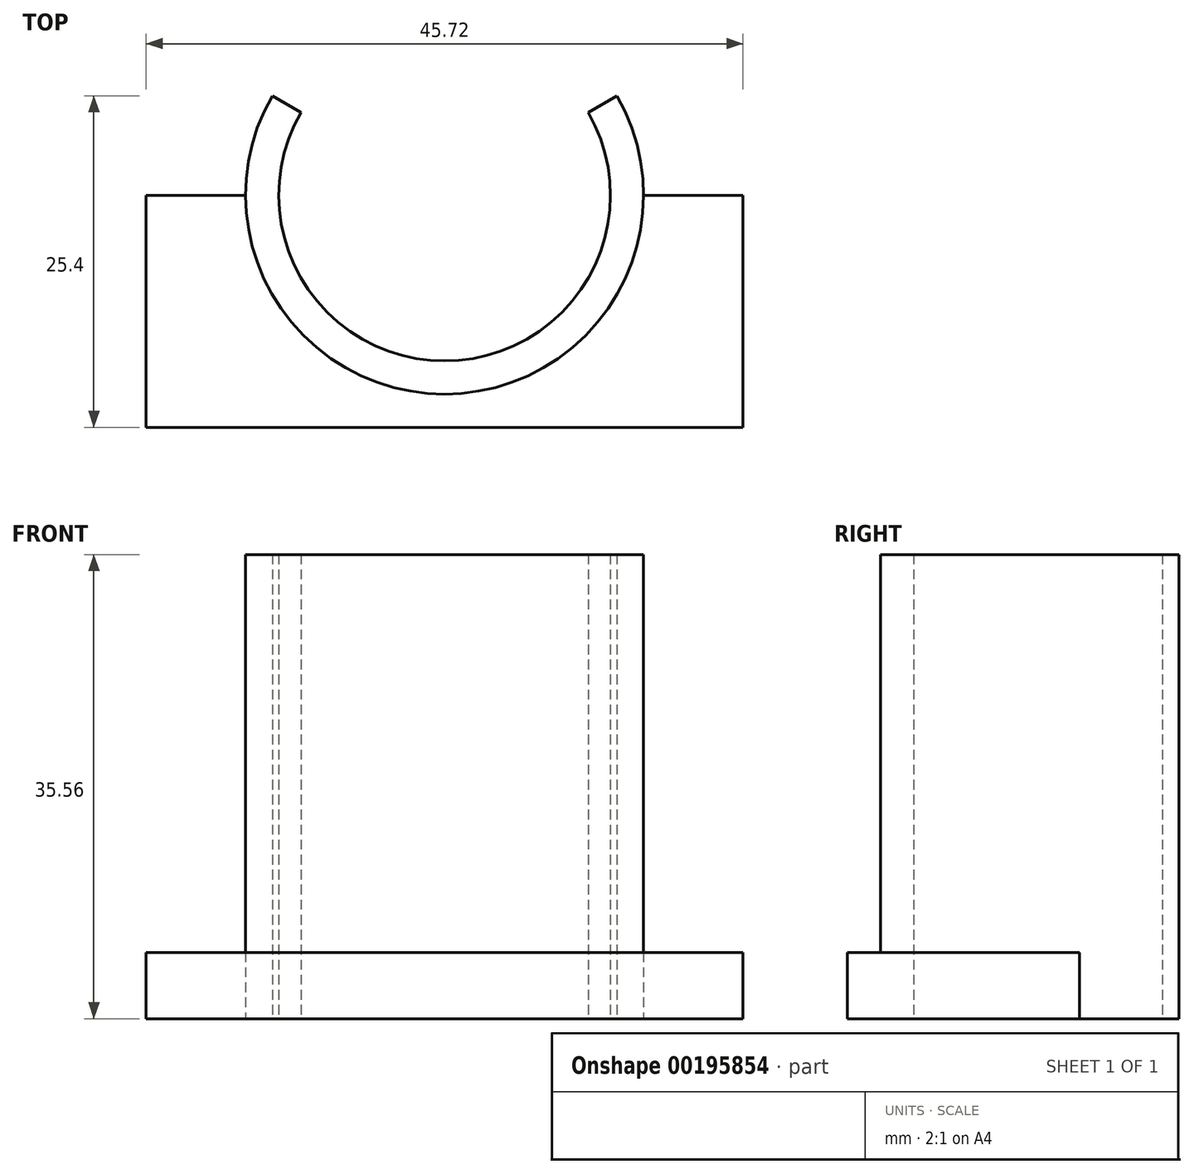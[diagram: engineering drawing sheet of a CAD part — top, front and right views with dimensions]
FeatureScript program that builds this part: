
annotation { "Feature Type Name" : "Feature", "Feature Type Description" : "" }
export const myFeature = defineFeature(function(context is Context, id is Id, definition is map)
    precondition{}
    {
        {
            var Q0;
            Q0=qCreatedBy(makeId("Top.planeOp"),FACE);
            var sketch = newSketch(context, id + "F0", { "sketchPlane" : qUnion([Q0])});
            skArc(sketch, "E0", {"start": v(-11, 6.35) * mm, "mid": v(0, -12.7) * mm, "end": v(11, 6.35) * mm});
            skArc(sketch, "E1", {"start": v(-13.2, 7.62) * mm, "mid": v(0, -15.24) * mm, "end": v(13.2, 7.62) * mm});
            skLineSegment(sketch, "E2", {"start": v(0, 0) * mm, "end": v(-15.24, 0) * mm, "construction": true});
            skLineSegment(sketch, "E3", {"start": v(-11, 6.35) * mm, "end": v(-13.2, 7.62) * mm});
            skLineSegment(sketch, "E4", {"start": v(11, 6.35) * mm, "end": v(13.2, 7.62) * mm});
            skSolve(sketch);
        }
        {
            var Q0;
            Q0 = qSketchRegion(id + "F0", true);
            extrude(context, id + "F1", {"entities" : qUnion([Q0]), "depth" : 35.56 * mm});
        }
        {
            var Q0;
            Q0=qCreatedBy(makeId("Top.planeOp"),FACE);
            var sketch = newSketch(context, id + "F2", { "sketchPlane" : qUnion([Q0])});
            skLineSegment(sketch, "E5.bottom", {"start": v(15.24, 0) * mm, "end": v(22.86, 0) * mm});
            skLineSegment(sketch, "E5.top", {"start": v(0, -17.78) * mm, "end": v(22.86, -17.78) * mm});
            skLineSegment(sketch, "E5.left", {"start": v(0, 0) * mm, "end": v(0, -17.78) * mm, "construction": true});
            skLineSegment(sketch, "E5.right", {"start": v(22.86, 0) * mm, "end": v(22.86, -17.78) * mm});
            skLineSegment(sketch, "E6.MirrorCS", {"start": v(-15.24, 0) * mm, "end": v(-22.86, 0) * mm});
            skLineSegment(sketch, "E7.MirrorCS", {"start": v(-22.86, 0) * mm, "end": v(-22.86, -17.78) * mm});
            skLineSegment(sketch, "E8.MirrorCS", {"start": v(0, -17.78) * mm, "end": v(-22.86, -17.78) * mm});
            skArc(sketch, "E9", {"start": v(-15.24, 0) * mm, "mid": v(0, -15.24) * mm, "end": v(15.24, 0) * mm});
            skSolve(sketch);
        }
        {
            var Q0;
            Q0 = qSketchRegion(id + "F2", true);
            extrude(context, id + "F3", {"entities" : qUnion([Q0]), "operationType" : NewBodyOperationType.ADD, "depth" : 5.08 * mm});
        }
    });
